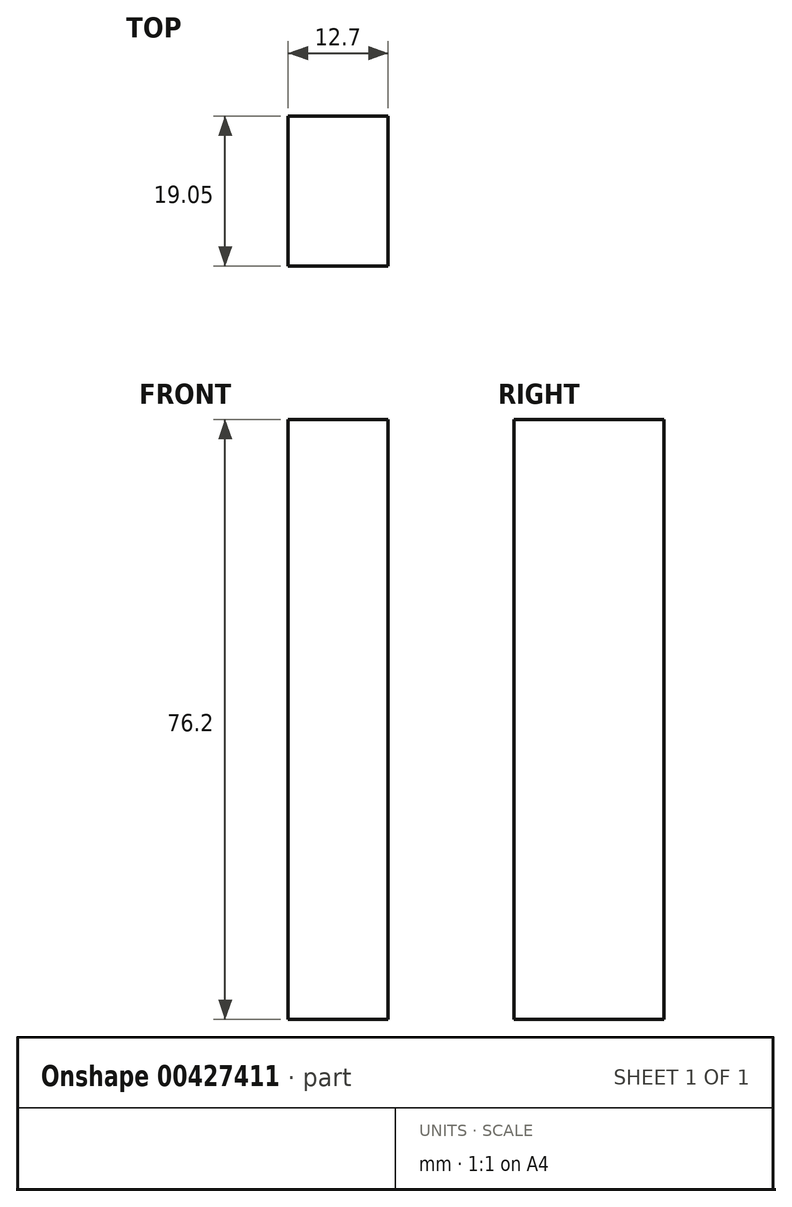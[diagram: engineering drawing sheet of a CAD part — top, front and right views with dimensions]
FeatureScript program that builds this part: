
annotation { "Feature Type Name" : "Feature", "Feature Type Description" : "" }
export const myFeature = defineFeature(function(context is Context, id is Id, definition is map)
    precondition{}
    {
        {
            var Q0;
            Q0=qCreatedBy(makeId("Top.planeOp"),FACE);
            var sketch = newSketch(context, id + "F0", { "sketchPlane" : qUnion([Q0])});
            skLineSegment(sketch, "E0.bottom", {"start": v(0, 0) * mm, "end": v(12.7, 0) * mm});
            skLineSegment(sketch, "E0.top", {"start": v(0, 19.05) * mm, "end": v(12.7, 19.05) * mm});
            skLineSegment(sketch, "E0.left", {"start": v(0, 0) * mm, "end": v(0, 19.05) * mm});
            skLineSegment(sketch, "E0.right", {"start": v(12.7, 0) * mm, "end": v(12.7, 19.05) * mm});
            skSolve(sketch);
        }
        {
            var Q0;
            Q0 = qSketchRegion(id + "F0", true);
            extrude(context, id + "F1", {"entities" : qUnion([Q0]), "depth" : 76.2 * mm});
        }
    });
